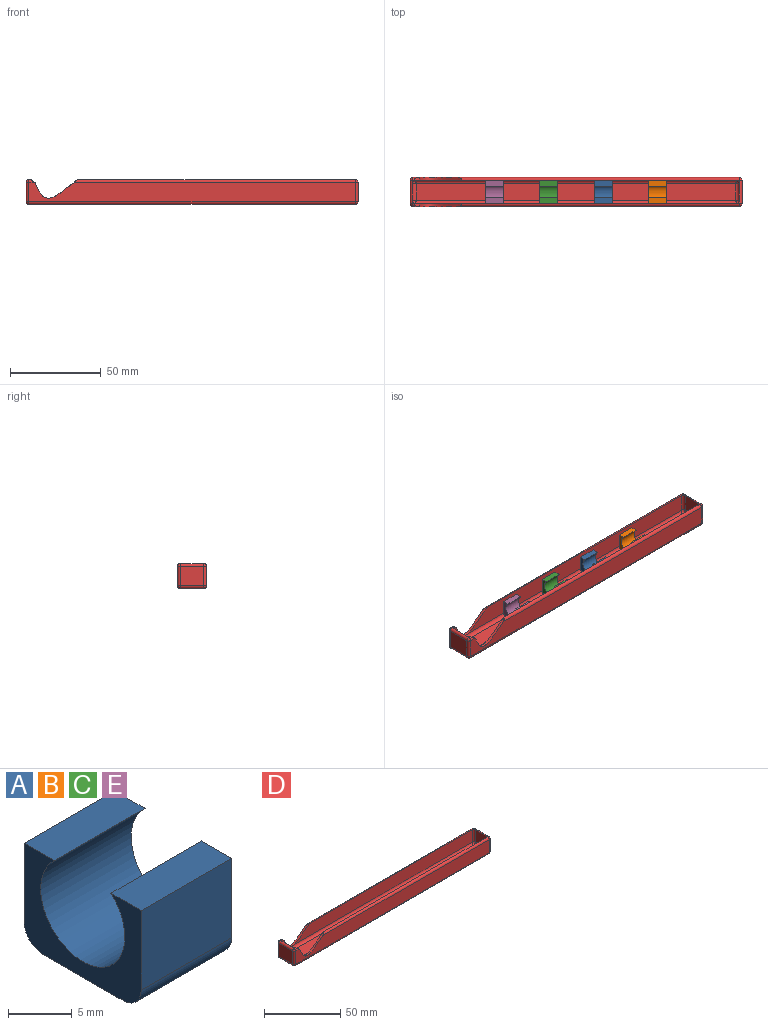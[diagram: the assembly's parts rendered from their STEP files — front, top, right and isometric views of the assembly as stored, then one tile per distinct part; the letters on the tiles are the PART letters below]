
ASSEMBLY  parts=5 mates=4
PART A: 10 faces, bbox 10x12.9x9.6 mm
  f0: plane 10x3.33mm, normal (0,0,1), area 33.3mm2, adj f1,f3,f4,f7
  f1: plane 12.9x9.6mm, normal (1,0,0), area 59.3mm2, adj f0,f2,f4,f5,f6,f7,f8,f9
  f2: plane 10x7.6mm, normal (0,1,0), area 76mm2, adj f1,f3,f5,f8
  f3: plane 12.9x9.6mm, normal (-1,0,0), area 59.3mm2, adj f0,f2,f4,f5,f6,f7,f8,f9
  f4: plane 10x7.6mm, normal (0,-1,0), area 76mm2, adj f0,f1,f3,f9
  f5: plane 10x3.33mm, normal (0,0,1), area 33.3mm2, adj f1,f2,f3,f7
  f6: plane 10x8.9mm, normal (0,0,-1), area 89mm2, adj f1,f3,f8,f9
  f7: cylinder r=4.65mm len=10mm, axis (-1,0,0), area 223.8mm2, adj f0,f1,f3,f5
  f8: cylinder r=2mm len=10mm, axis (-1,0,0), area 31.4mm2, adj f1,f2,f3,f6
  f9: cylinder r=2mm len=10mm, axis (1,0,0), area 31.4mm2, adj f1,f3,f4,f6
PART B: same geometry as A
PART C: same geometry as A
PART D: 52 faces, bbox 183x16x13.7 mm
  f0: plane 180x10.72mm, normal (0,1,0), area 1807.8mm2, adj f4,f25,f34,f35,f39,f49,f51
  f1: plane 9.99x8.16mm, normal (0,-1,0), area 35.3mm2, adj f5,f18,f49,f51
  f2: plane 9.99x8.16mm, normal (0,1,0), area 35.3mm2, adj f6,f17,f46,f48
  f3: cylinder r=1.5mm len=3.13mm, axis (-1,0,0), area 4.4mm2, adj f6,f9,f21,f24,f46
  f4: cylinder r=1.5mm len=3.13mm, axis (1,0,0), area 4.4mm2, adj f0,f5,f24,f30,f51
  f5: cylinder r=1.5mm len=10mm, axis (0,0,1), area 23.4mm2, adj f1,f4,f13,f24,f44,f51
  f6: cylinder r=1.5mm len=10mm, axis (0,0,-1), area 23.4mm2, adj f2,f3,f13,f24,f45,f46
  f7: plane 13x10.7mm, normal (1,0,0), area 139.1mm2, adj f28,f33,f36,f39
  f8: plane 13x10.7mm, normal (-1,0,0), area 139.1mm2, adj f20,f24,f25,f26
  f9: plane 180x10.72mm, normal (0,-1,0), area 1807.8mm2, adj f3,f20,f23,f27,f28,f46,f48
  f10: plane 180x13mm, normal (0,0,-1), area 2340mm2, adj f26,f27,f35,f36
  f11: plane 10x10mm, normal (-1,0,0), area 100mm2, adj f16,f33,f40,f42
  f12: plane 166.39x10.33mm, normal (0,-1,0), area 1581.2mm2, adj f18,f34,f42,f49,f50
  f13: plane 10x10mm, normal (1,0,0), area 100mm2, adj f5,f6,f19,f24
  f14: plane 166.39x10.33mm, normal (0,1,0), area 1581.2mm2, adj f17,f23,f40,f47,f48
  f15: plane 176x9mm, normal (0,0,1), area 1584mm2, adj f16,f17,f18,f19
  f16: cylinder r=2mm len=10mm, axis (0,1,0), area 29.8mm2, adj f11,f15,f41,f43
  f17: cylinder r=2mm len=177mm, axis (1,0,0), area 553.9mm2, adj f2,f14,f15,f41,f45,f48
  f18: cylinder r=2mm len=177mm, axis (-1,0,0), area 553.9mm2, adj f1,f12,f15,f43,f44,f49
  f19: cylinder r=2mm len=10mm, axis (0,-1,0), area 29.8mm2, adj f13,f15,f44,f45
  f20: cylinder r=1.5mm len=10.7mm, axis (0,0,1), area 25.2mm2, adj f8,f9,f21,f22
  f21: sphere r=1.5mm, area 3.5mm2, adj f3,f20,f24
  f22: sphere r=1.5mm, area 3.5mm2, adj f20,f26,f27
  f23: cylinder r=1.5mm len=154.94mm, axis (-1,0,0), area 362.7mm2, adj f9,f14,f29,f33,f40,f47
  f24: cylinder r=1.5mm len=13mm, axis (0,1,0), area 31.3mm2, adj f3,f4,f5,f6,f8,f13,f21,f30
  f25: cylinder r=1.5mm len=10.7mm, axis (0,0,-1), area 25.2mm2, adj f0,f8,f30,f31
  f26: cylinder r=1.5mm len=13mm, axis (0,-1,0), area 30.6mm2, adj f8,f10,f22,f31
  f27: cylinder r=1.5mm len=180mm, axis (1,0,0), area 424.1mm2, adj f9,f10,f22,f32
  f28: cylinder r=1.5mm len=10.7mm, axis (0,0,-1), area 25.2mm2, adj f7,f9,f29,f32
  f29: sphere r=1.5mm, area 3.5mm2, adj f23,f28,f33
  f30: sphere r=1.5mm, area 3.5mm2, adj f4,f24,f25
  f31: sphere r=1.5mm, area 3.5mm2, adj f25,f26,f35
  f32: sphere r=1.5mm, area 3.5mm2, adj f27,f28,f36
  f33: cylinder r=1.5mm len=13mm, axis (0,-1,0), area 31.3mm2, adj f7,f11,f23,f29,f34,f37,f40,f42
  f34: cylinder r=1.5mm len=154.94mm, axis (1,0,0), area 362.7mm2, adj f0,f12,f33,f37,f42,f50
  f35: cylinder r=1.5mm len=180mm, axis (-1,0,0), area 424.1mm2, adj f0,f10,f31,f38
  f36: cylinder r=1.5mm len=13mm, axis (0,1,0), area 30.6mm2, adj f7,f10,f32,f38
  f37: sphere r=1.5mm, area 3.5mm2, adj f33,f34,f39
  f38: sphere r=1.5mm, area 3.5mm2, adj f35,f36,f39
  f39: cylinder r=1.5mm len=10.7mm, axis (0,0,1), area 25.2mm2, adj f0,f7,f37,f38
  f40: cylinder r=1.5mm len=10mm, axis (0,0,1), area 23.5mm2, adj f11,f14,f23,f33,f41
  f41: bspline ~2.45x2mm, area 4.8mm2, adj f16,f17,f40
  f42: cylinder r=1.5mm len=10mm, axis (0,0,-1), area 23.5mm2, adj f11,f12,f33,f34,f43
  f43: bspline ~2.45x2mm, area 4.8mm2, adj f16,f18,f42
  f44: bspline ~2.45x2mm, area 4.8mm2, adj f5,f18,f19
  f45: bspline ~2.45x2mm, area 4.8mm2, adj f6,f17,f19
  f46: extruded ~2.59x2.07mm, area 4.3mm2, adj f2,f3,f6,f9,f48
  f47: extruded ~1.91x1.5mm, area 2.8mm2, adj f14,f23,f48
  f48: extruded ~21.39x8.76mm, area 42.7mm2, adj f2,f9,f14,f17,f46,f47
  f49: extruded ~21.39x8.76mm, area 42.7mm2, adj f0,f1,f12,f18,f50,f51
  f50: extruded ~1.91x1.5mm, area 2.8mm2, adj f12,f34,f49
  f51: extruded ~2.59x2.07mm, area 4.3mm2, adj f0,f1,f4,f5,f49
PART E: same geometry as A
PLACE A t=(15.8,0.67,-5.09)mm
PLACE B t=(45.8,0.67,-5.09)mm
PLACE C t=(-14.2,0.67,-5.09)mm
PLACE D t=(0.8,0.67,-6.79)mm
PLACE E t=(-44.2,0.67,-5.09)mm
MATE fastened B.f6 <-> D.f15  axis (0,0,-1) through (45.8,0.67,-5.09)mm
MATE fastened A.f6 <-> D.f15  axis (0,0,-1) through (15.8,0.67,-5.09)mm
MATE fastened C.f6 <-> D.f15  axis (0,0,-1) through (-14.2,0.67,-5.09)mm
MATE fastened E.f6 <-> D.f15  axis (0,0,-1) through (-44.2,0.67,-5.09)mm
